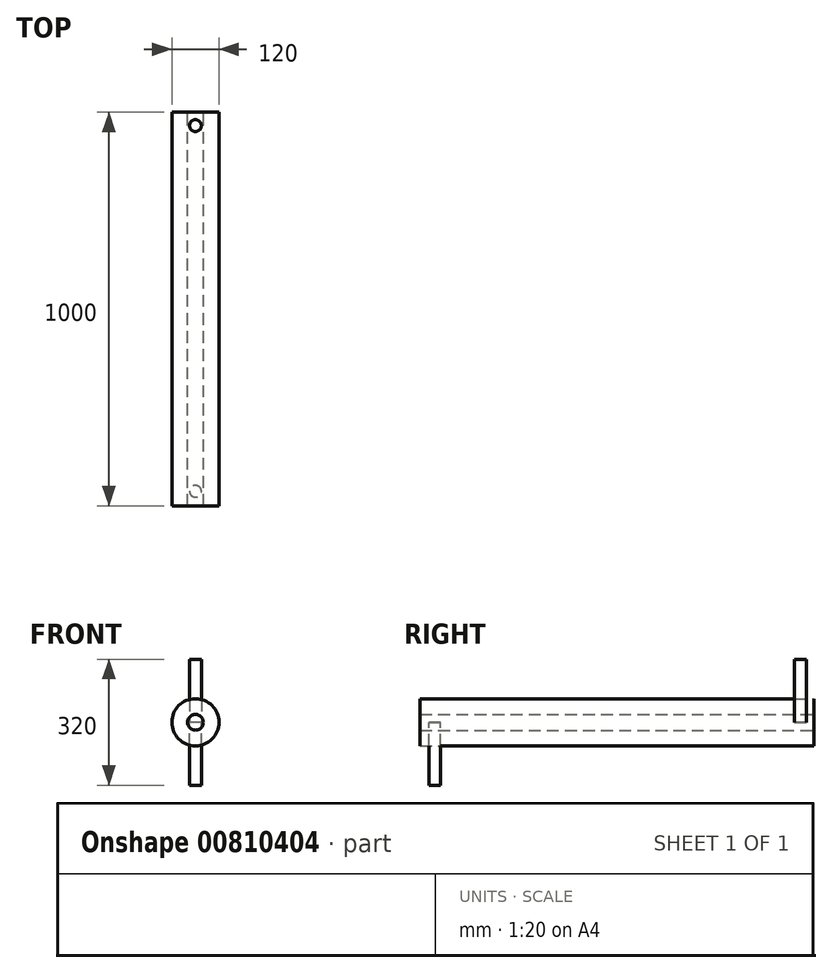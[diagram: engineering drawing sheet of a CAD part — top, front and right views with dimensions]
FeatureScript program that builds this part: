
annotation { "Feature Type Name" : "Feature", "Feature Type Description" : "" }
export const myFeature = defineFeature(function(context is Context, id is Id, definition is map)
    precondition{}
    {
        {
            var Q0;
            Q0=qCreatedBy(makeId("Front.planeOp"),FACE);
            var sketch = newSketch(context, id + "F0", { "sketchPlane" : qUnion([Q0])});
            skCircle(sketch, "E0", {"center": v(0, 0) * mm, "radius": 60 * mm});
            skSolve(sketch);
        }
        {
            var Q0;
            Q0=qCreatedBy(makeId("Front.planeOp"),FACE);
            var sketch = newSketch(context, id + "F1", { "sketchPlane" : qUnion([Q0])});
            skCircle(sketch, "E1", {"center": v(0, 0) * mm, "radius": 20 * mm});
            skSolve(sketch);
        }
        {
            var Q0;
            Q0=makeQuery(id+"F0.imprint","IMPRINT",FACE,{"disambiguationData":[TD([[makeQuery(id+"F0.imprint","IMPRINT",EDGE,{"derivedFrom":sQuery(id+"F0.wireOp",EDGE,"E0")}),1.0]])]});
            var Q1;
            Q1=makeQuery(id+"F1.imprint","IMPRINT",FACE,{"disambiguationData":[TD([[makeQuery(id+"F1.imprint","IMPRINT",EDGE,{"derivedFrom":sQuery(id+"F1.wireOp",EDGE,"E1")}),1.0]])]});
            extrude(context, id + "F2", {"entities" : qUnion([Q0, Q1]), "depth" : 1000 * mm, "offsetDistance" : 25 * mm});
        }
        {
            var Q0;
            Q0=qCreatedBy(makeId("Top.planeOp"),FACE);
            var sketch = newSketch(context, id + "F3", { "sketchPlane" : qUnion([Q0])});
            skCircle(sketch, "E2", {"center": v(0, -33.89) * mm, "radius": 15 * mm});
            skSolve(sketch);
        }
        {
            var Q0;
            Q0=qSketchRegion(id+"F3",true);
            extrude(context, id + "F4", {"entities" : qUnion([Q0]), "depth" : 160 * mm, "offsetDistance" : 25 * mm});
        }
        {
            var Q0;
            Q0=qCreatedBy(makeId("Top.planeOp"),FACE);
            var sketch = newSketch(context, id + "F5", { "sketchPlane" : qUnion([Q0])});
            skCircle(sketch, "E3", {"center": v(0, -962.96) * mm, "radius": 15 * mm});
            skSolve(sketch);
        }
        {
            var Q0;
            Q0=qSketchRegion(id+"F5",true);
            extrude(context, id + "F6", {"entities" : qUnion([Q0]), "oppositeDirection" : true, "depth" : 160 * mm, "offsetDistance" : 25 * mm});
        }
    });
